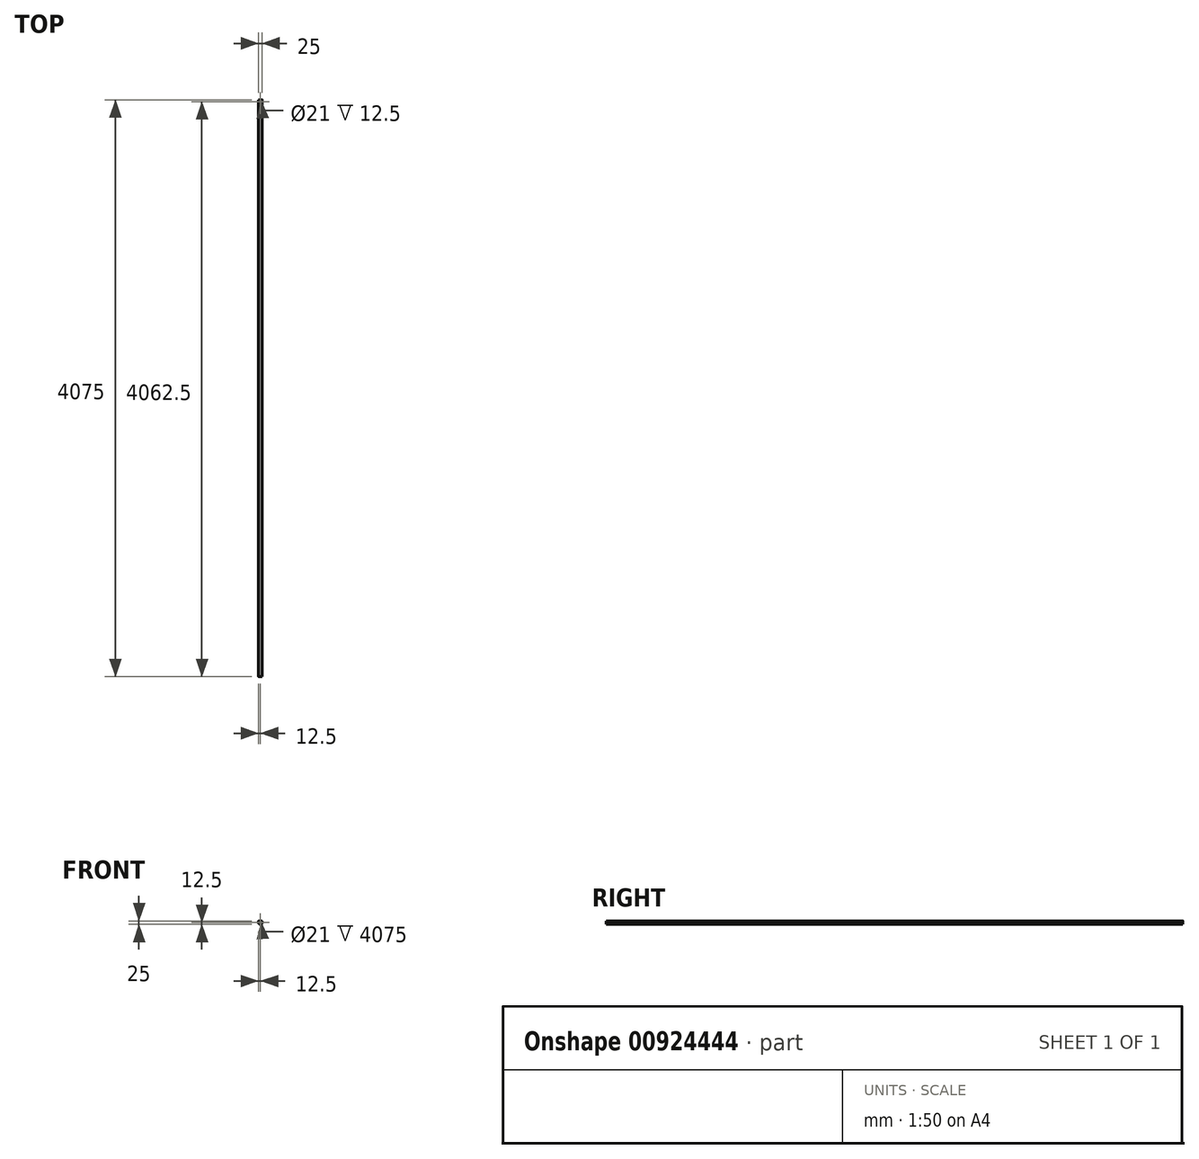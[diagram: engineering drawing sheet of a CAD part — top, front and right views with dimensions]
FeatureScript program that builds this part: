
annotation { "Feature Type Name" : "Feature", "Feature Type Description" : "" }
export const myFeature = defineFeature(function(context is Context, id is Id, definition is map)
    precondition{}
    {
        {
            var Q0;
            Q0=qCreatedBy(makeId("Front.planeOp"),FACE);
            var sketch = newSketch(context, id + "F0", { "sketchPlane" : qUnion([Q0])});
            skCircle(sketch, "E0", {"center": v(0, 0) * mm, "radius": 12.5 * mm});
            skSolve(sketch);
        }
        {
            var Q0;
            Q0=qSketchRegion(id+"F0",true);
            extrude(context, id + "F1", {"entities" : qUnion([Q0]), "depth" : 4075 * mm, "offsetDistance" : 25 * mm});
        }
        {
            var Q0;
            Q0=makeQuery(id+"F1.opExtrude","CAP_FACE",FACE,{"disambiguationData":[OSD([sQuery(id+"F0.wireOp",EDGE,"E0")])],"isStart":false});
            var sketch = newSketch(context, id + "F2", { "sketchPlane" : qUnion([Q0])});
            skCircle(sketch, "E1", {"center": v(0, 0) * mm, "radius": 10.5 * mm});
            skSolve(sketch);
        }
        {
            var Q0;
            Q0=qSketchRegion(id+"F2",true);
            extrude(context, id + "F3", {"entities" : qUnion([Q0]), "operationType" : NewBodyOperationType.REMOVE, "oppositeDirection" : true, "depth" : 4050 * mm, "offsetDistance" : 25 * mm});
        }
        {
            var Q0;
            Q0=qCreatedBy(makeId("Top.planeOp"),FACE);
            var sketch = newSketch(context, id + "F4", { "sketchPlane" : qUnion([Q0])});
            skCircle(sketch, "E2", {"center": v(0, -12.5) * mm, "radius": 12.5 * mm});
            skSolve(sketch);
        }
        {
            var Q0;
            Q0=qSketchRegion(id+"F4",true);
            extrude(context, id + "F5", {"entities" : qUnion([Q0]), "operationType" : NewBodyOperationType.ADD, "depth" : 12.5 * mm, "offsetDistance" : 25 * mm});
        }
        {
            var Q0;
            Q0=makeQuery(id+"F5.opExtrude","CAP_FACE",FACE,{"disambiguationData":[OSD([sQuery(id+"F4.wireOp",EDGE,"E2")])],"isStart":false});
            var sketch = newSketch(context, id + "F6", { "sketchPlane" : qUnion([Q0])});
            skCircle(sketch, "E3", {"center": v(0, -12.5) * mm, "radius": 10.5 * mm});
            skSolve(sketch);
        }
        {
            var Q0;
            Q0=qSketchRegion(id+"F6",true);
            extrude(context, id + "F7", {"entities" : qUnion([Q0]), "operationType" : NewBodyOperationType.REMOVE, "oppositeDirection" : true, "depth" : 12.5 * mm, "offsetDistance" : 25 * mm});
        }
        {
            var Q0;
            Q0=qCreatedBy(makeId("Front.planeOp"),FACE);
            var sketch = newSketch(context, id + "F8", { "sketchPlane" : qUnion([Q0])});
            skCircle(sketch, "E4", {"center": v(0, 0) * mm, "radius": 10.5 * mm});
            skSolve(sketch);
        }
        {
            var Q0;
            Q0=qSketchRegion(id+"F8",true);
            extrude(context, id + "F9", {"entities" : qUnion([Q0]), "operationType" : NewBodyOperationType.REMOVE, "depth" : 600 * mm, "offsetDistance" : 25 * mm});
        }
    });
